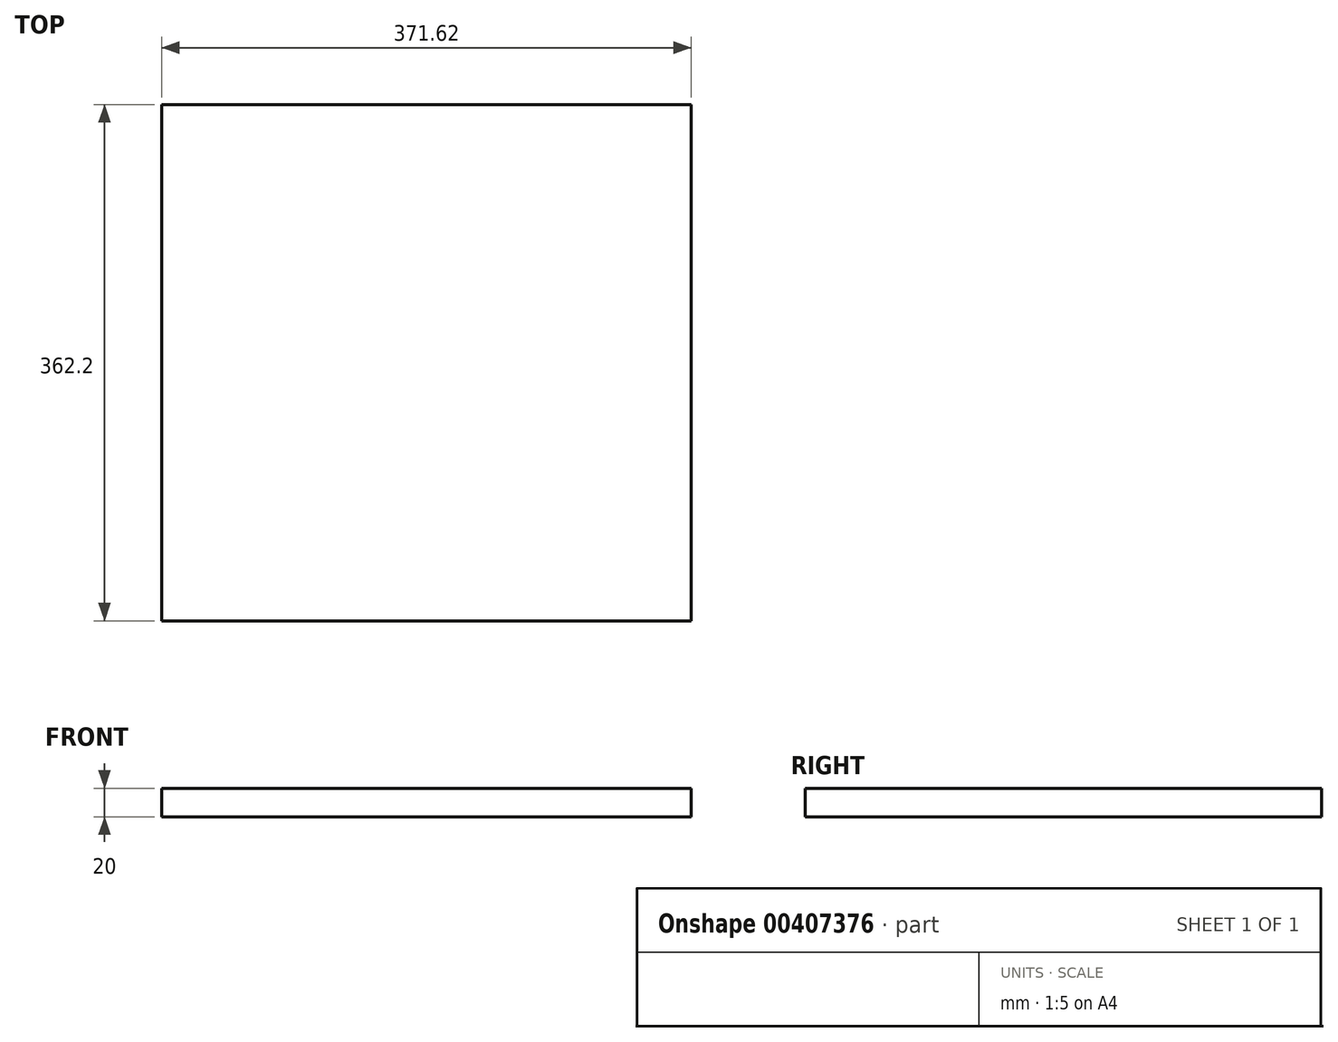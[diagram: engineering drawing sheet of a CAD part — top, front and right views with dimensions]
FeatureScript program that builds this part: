
annotation { "Feature Type Name" : "Feature", "Feature Type Description" : "" }
export const myFeature = defineFeature(function(context is Context, id is Id, definition is map)
    precondition{}
    {
        {
            var Q0;
            Q0=qCreatedBy(makeId("Top.planeOp"),FACE);
            var sketch = newSketch(context, id + "F0", { "sketchPlane" : qUnion([Q0])});
            skLineSegment(sketch, "E0.bottom", {"start": v(185.8, -181.1) * mm, "end": v(-185.8, -181.1) * mm});
            skLineSegment(sketch, "E0.top", {"start": v(185.8, 181.1) * mm, "end": v(-185.8, 181.1) * mm});
            skLineSegment(sketch, "E0.left", {"start": v(185.8, -181.1) * mm, "end": v(185.8, 181.1) * mm});
            skLineSegment(sketch, "E0.right", {"start": v(-185.8, -181.1) * mm, "end": v(-185.8, 181.1) * mm});
            skPoint(sketch, "E0.middle", {"position": v(0, 0) * mm});
            skSolve(sketch);
        }
        {
            var Q0;
            Q0=makeQuery(id+"F0.imprint","IMPRINT",FACE,{"disambiguationData":[TD([[makeQuery(id+"F0.imprint","IMPRINT",EDGE,{"derivedFrom":sQuery(id+"F0.wireOp",EDGE,"E0.bottom")}),-1.0]])]});
            extrude(context, id + "F1", {"entities" : qUnion([Q0]), "depth" : 20 * mm, "offsetDistance" : 25 * mm});
        }
    });
